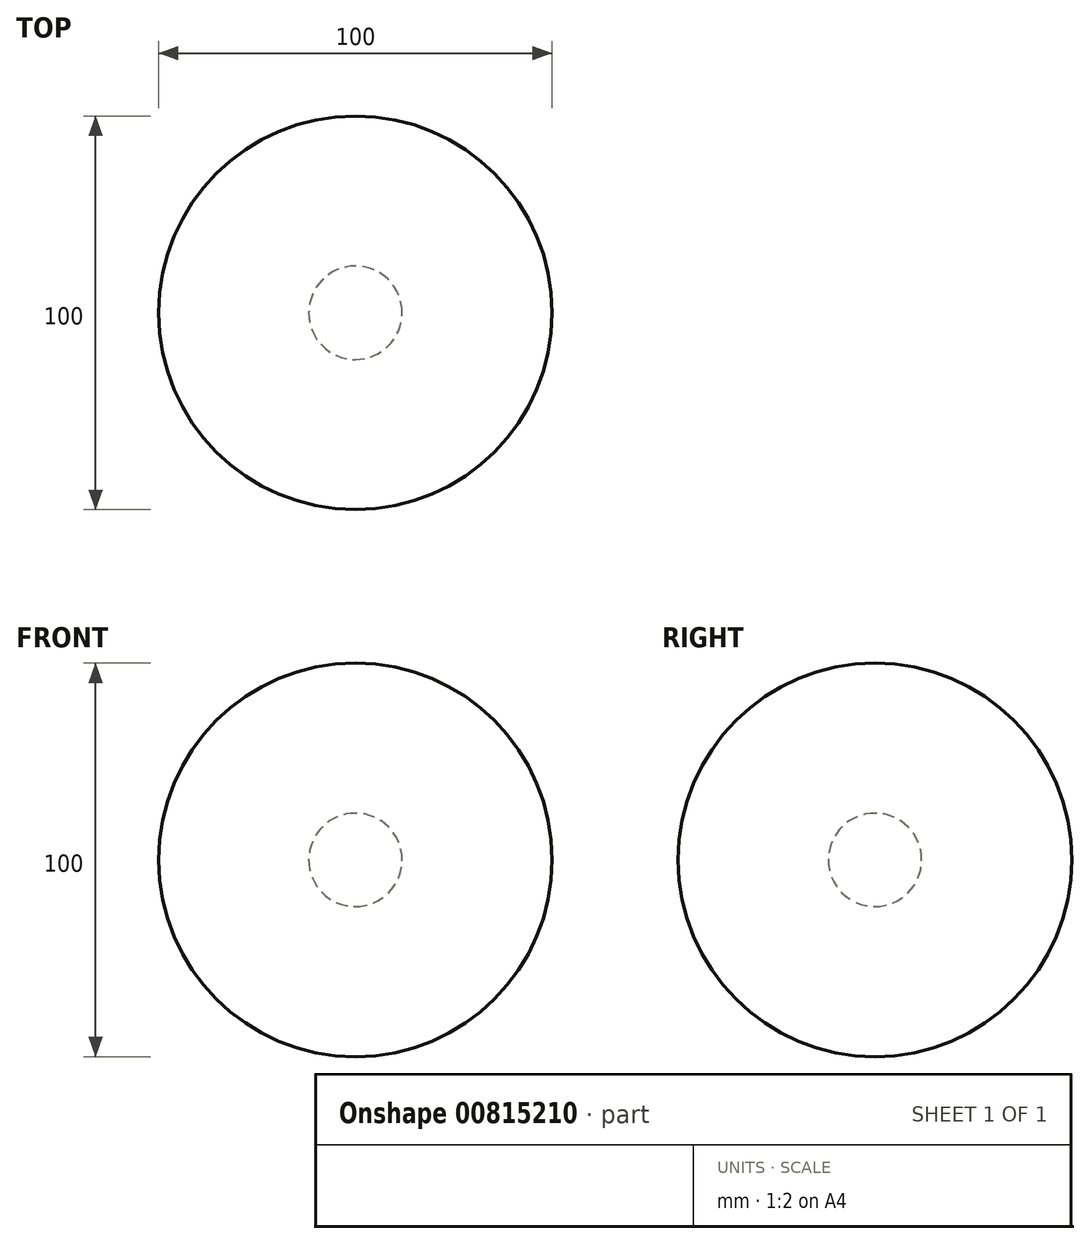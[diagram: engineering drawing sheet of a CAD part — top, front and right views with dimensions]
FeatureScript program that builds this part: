
annotation { "Feature Type Name" : "Feature", "Feature Type Description" : "" }
export const myFeature = defineFeature(function(context is Context, id is Id, definition is map)
    precondition{}
    {
        {
            var Q0;
            Q0=qCreatedBy(makeId("Front.planeOp"),FACE);
            var sketch = newSketch(context, id + "F0", { "sketchPlane" : qUnion([Q0])});
            skCircle(sketch, "E0", {"center": v(0, 0) * mm, "radius": 50 * mm});
            skLineSegment(sketch, "E1", {"start": v(0, 50) * mm, "end": v(0, -50) * mm});
            skCircle(sketch, "E2", {"center": v(0, 0) * mm, "radius": 11.86 * mm});
            skSolve(sketch);
        }
        {
            var Q0;
            {var subQ0=sQuery(id+"F0.wireOp",EDGE,"E1");Q0=makeQuery(id+"F0.imprint","IMPRINT",FACE,{"disambiguationData":[TD([[makeQuery(id+"F0.imprint","IMPRINT",EDGE,{"derivedFrom":subQ0}),1.0]])]});}
            var Q1;
            Q1=sQuery(id+"F0.wireOp",EDGE,"E1");
            revolve(context, id + "F1", {"surfaceOperationType" : NewSurfaceOperationType.NEW, "entities" : qUnion([Q0]), "axis" : qUnion([Q1]), "revolveType" : RevolveType.FULL});
        }
    });
